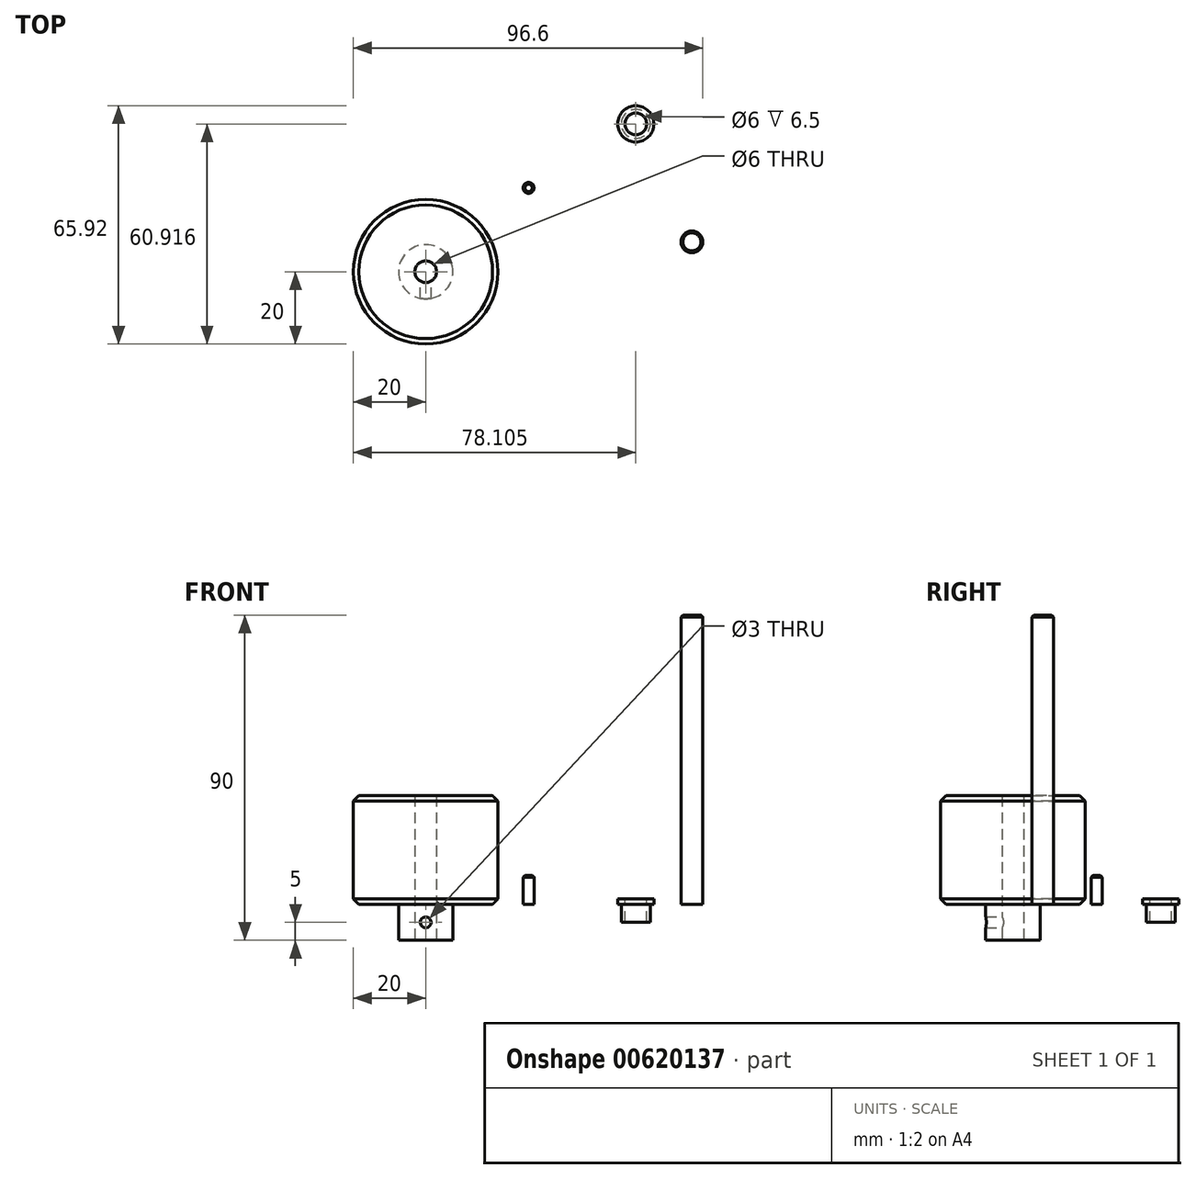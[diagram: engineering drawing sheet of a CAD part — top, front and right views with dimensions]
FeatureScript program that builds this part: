
annotation { "Feature Type Name" : "Feature", "Feature Type Description" : "" }
export const myFeature = defineFeature(function(context is Context, id is Id, definition is map)
    precondition{}
    {
        {
            var Q0;
            Q0=qCreatedBy(makeId("Top.planeOp"),FACE);
            var sketch = newSketch(context, id + "F0", { "sketchPlane" : qUnion([Q0])});
            skCircle(sketch, "E0", {"center": v(0, 0) * mm, "radius": 3 * mm});
            skCircle(sketch, "E1", {"center": v(0, 0) * mm, "radius": 7.5 * mm});
            skCircle(sketch, "E2", {"center": v(0, 0) * mm, "radius": 20 * mm});
            skCircle(sketch, "E3", {"center": v(73.6, 8.26) * mm, "radius": 3 * mm});
            skCircle(sketch, "E4", {"center": v(58.1, 40.92) * mm, "radius": 3 * mm});
            skCircle(sketch, "E5", {"center": v(58.1, 40.92) * mm, "radius": 4 * mm});
            skCircle(sketch, "E6", {"center": v(58.1, 40.92) * mm, "radius": 5 * mm});
            skCircle(sketch, "E7", {"center": v(28.46, 23.2) * mm, "radius": 1.5 * mm});
            skSolve(sketch);
        }
        {
            var Q0;
            Q0=makeQuery(id+"F0.imprint","IMPRINT",FACE,{"disambiguationData":[TD([[makeQuery(id+"F0.imprint","IMPRINT",EDGE,{"derivedFrom":sQuery(id+"F0.wireOp",EDGE,"E0")}),-1.0]])]});
            var Q1;
            Q1=makeQuery(id+"F0.imprint","IMPRINT",FACE,{"disambiguationData":[TD([[makeQuery(id+"F0.imprint","IMPRINT",EDGE,{"derivedFrom":sQuery(id+"F0.wireOp",EDGE,"E1")}),-1.0]])]});
            extrude(context, id + "F1", {"entities" : qUnion([Q0, Q1]), "depth" : 30 * mm, "offsetDistance" : 25 * mm});
        }
        {
            var Q0;
            Q0=makeQuery(id+"F0.imprint","IMPRINT",FACE,{"disambiguationData":[TD([[makeQuery(id+"F0.imprint","IMPRINT",EDGE,{"derivedFrom":sQuery(id+"F0.wireOp",EDGE,"E0")}),-1.0]])]});
            extrude(context, id + "F2", {"entities" : qUnion([Q0]), "operationType" : NewBodyOperationType.ADD, "oppositeDirection" : true, "depth" : 10 * mm, "offsetDistance" : 25 * mm});
        }
        {
            var Q0;
            Q0=makeQuery(id+"F1.opExtrude","CAP_EDGE",EDGE,{"disambiguationData":[OSD([sQuery(id+"F0.wireOp",EDGE,"E2")])],"isStart":false});
            var Q1;
            Q1=makeQuery(id+"F1.opExtrude","CAP_EDGE",EDGE,{"disambiguationData":[OSD([sQuery(id+"F0.wireOp",EDGE,"E2")])],"isStart":true});
            chamfer(context, id + "F3", {"entities" : qUnion([Q0, Q1]), "width" : 1.5 * mm, "tangentPropagation" : true});
        }
        {
            var Q0;
            Q0=qCreatedBy(makeId("Front.planeOp"),FACE);
            var sketch = newSketch(context, id + "F4", { "sketchPlane" : qUnion([Q0])});
            skLineSegment(sketch, "E8.0", {"start": v(-7.5, -10) * mm, "end": v(7.5, -10) * mm});
            skLineSegment(sketch, "E9.0", {"start": v(-7.5, 0) * mm, "end": v(7.5, 0) * mm});
            skLineSegment(sketch, "E10", {"start": v(-7.5, -10) * mm, "end": v(-7.5, 0) * mm});
            skLineSegment(sketch, "E11", {"start": v(7.5, -10) * mm, "end": v(7.5, 0) * mm});
            skLineSegment(sketch, "E12", {"start": v(0, -10) * mm, "end": v(0, 0) * mm, "construction": true});
            skLineSegment(sketch, "E13", {"start": v(-7.5, -5) * mm, "end": v(7.5, -5) * mm, "construction": true});
            skCircle(sketch, "E14", {"center": v(0, -5) * mm, "radius": 1.5 * mm});
            skSolve(sketch);
        }
        {
            var Q0;
            Q0=makeQuery(id+"F4.imprint","IMPRINT",FACE,{"disambiguationData":[TD([[makeQuery(id+"F4.imprint","IMPRINT",EDGE,{"derivedFrom":sQuery(id+"F4.wireOp",EDGE,"E14")}),1.0]])]});
            var Q1;
            Q1=makeQuery(id+"F2.opExtrude","SWEPT_FACE",FACE,{"disambiguationData":[OSD([sQuery(id+"F0.wireOp",EDGE,"E1")])]});
            extrude(context, id + "F5", {"entities" : qUnion([Q0]), "operationType" : NewBodyOperationType.REMOVE, "endBound" : BoundingType.UP_TO_SURFACE, "depth" : 25 * mm, "endBoundEntityFace" : qUnion([Q1]), "offsetDistance" : 25 * mm});
        }
        {
            var Q0;
            Q0=makeQuery(id+"F0.imprint","IMPRINT",FACE,{"disambiguationData":[TD([[makeQuery(id+"F0.imprint","IMPRINT",EDGE,{"derivedFrom":sQuery(id+"F0.wireOp",EDGE,"E3")}),1.0]])]});
            extrude(context, id + "F6", {"entities" : qUnion([Q0]), "depth" : 80 * mm, "offsetDistance" : 25 * mm});
        }
        {
            var Q0;
            Q0=makeQuery(id+"F6.opExtrude","CAP_EDGE",EDGE,{"disambiguationData":[OSD([sQuery(id+"F0.wireOp",EDGE,"E3")])],"isStart":false});
            chamfer(context, id + "F7", {"entities" : qUnion([Q0]), "width" : .5 * mm, "tangentPropagation" : true});
        }
        {
            var Q0;
            Q0=makeQuery(id+"F0.imprint","IMPRINT",FACE,{"disambiguationData":[TD([[makeQuery(id+"F0.imprint","IMPRINT",EDGE,{"derivedFrom":sQuery(id+"F0.wireOp",EDGE,"E4")}),-1.0]])]});
            extrude(context, id + "F8", {"entities" : qUnion([Q0]), "oppositeDirection" : true, "depth" : 5 * mm, "offsetDistance" : 25 * mm});
        }
        {
            var Q0;
            Q0=makeQuery(id+"F0.imprint","IMPRINT",FACE,{"disambiguationData":[TD([[makeQuery(id+"F0.imprint","IMPRINT",EDGE,{"derivedFrom":sQuery(id+"F0.wireOp",EDGE,"E5")}),-1.0]])]});
            var Q1;
            Q1=makeQuery(id+"F0.imprint","IMPRINT",FACE,{"disambiguationData":[TD([[makeQuery(id+"F0.imprint","IMPRINT",EDGE,{"derivedFrom":sQuery(id+"F0.wireOp",EDGE,"E4")}),-1.0]])]});
            extrude(context, id + "F9", {"entities" : qUnion([Q0, Q1]), "operationType" : NewBodyOperationType.ADD, "depth" : 1.5 * mm, "offsetDistance" : 25 * mm});
        }
        {
            var Q0;
            Q0=makeQuery(id+"F0.imprint","IMPRINT",FACE,{"disambiguationData":[TD([[makeQuery(id+"F0.imprint","IMPRINT",EDGE,{"derivedFrom":sQuery(id+"F0.wireOp",EDGE,"E7")}),1.0]])]});
            extrude(context, id + "F10", {"entities" : qUnion([Q0]), "depth" : 8 * mm, "offsetDistance" : 25 * mm});
        }
        {
            var Q0;
            Q0=makeQuery(id+"F10.opExtrude","CAP_EDGE",EDGE,{"disambiguationData":[OSD([sQuery(id+"F0.wireOp",EDGE,"E7")])],"isStart":false});
            chamfer(context, id + "F11", {"entities" : qUnion([Q0]), "width" : .5 * mm, "tangentPropagation" : true});
        }
    });
